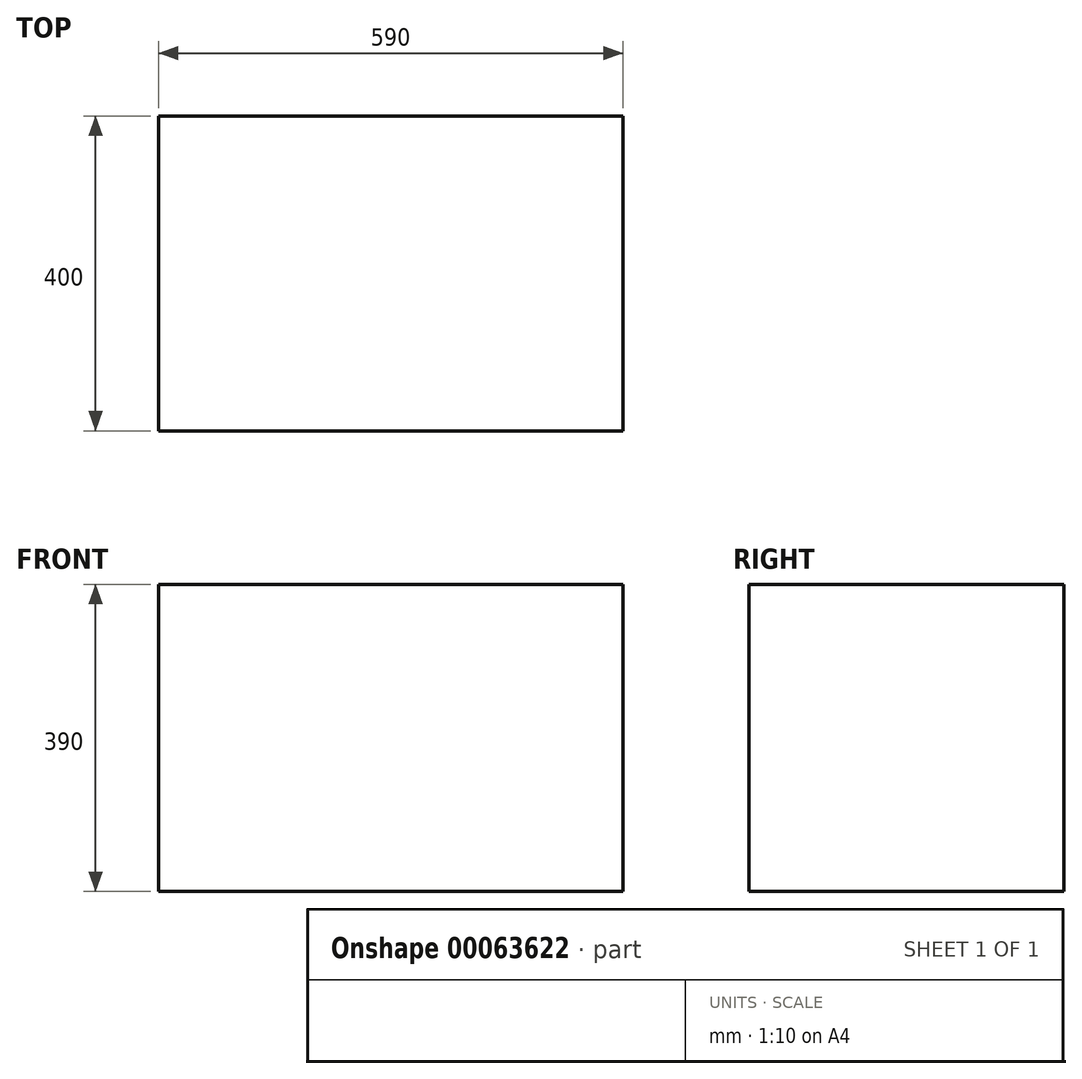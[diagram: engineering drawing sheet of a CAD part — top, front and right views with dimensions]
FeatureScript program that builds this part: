
annotation { "Feature Type Name" : "Feature", "Feature Type Description" : "" }
export const myFeature = defineFeature(function(context is Context, id is Id, definition is map)
    precondition{}
    {
        {
            var Q0;
            Q0=qCreatedBy(makeId("Top.planeOp"),FACE);
            var sketch = newSketch(context, id + "F0", { "sketchPlane" : qUnion([Q0])});
            skLineSegment(sketch, "E0.bottom", {"start": v(0, 0) * mm, "end": v(590, 0) * mm});
            skLineSegment(sketch, "E0.top", {"start": v(0, -400) * mm, "end": v(590, -400) * mm});
            skLineSegment(sketch, "E0.left", {"start": v(0, 0) * mm, "end": v(0, -400) * mm});
            skLineSegment(sketch, "E0.right", {"start": v(590, 0) * mm, "end": v(590, -400) * mm});
            skSolve(sketch);
        }
        {
            var Q0;
            Q0=makeQuery(id+"F0.imprint","IMPRINT",FACE,{"disambiguationData":[TD([[makeQuery(id+"F0.imprint","IMPRINT",EDGE,{"derivedFrom":sQuery(id+"F0.wireOp",EDGE,"E0.bottom")}),-1.0]])]});
            extrude(context, id + "F1", {"entities" : qUnion([Q0]), "depth" : 390 * mm});
        }
    });
